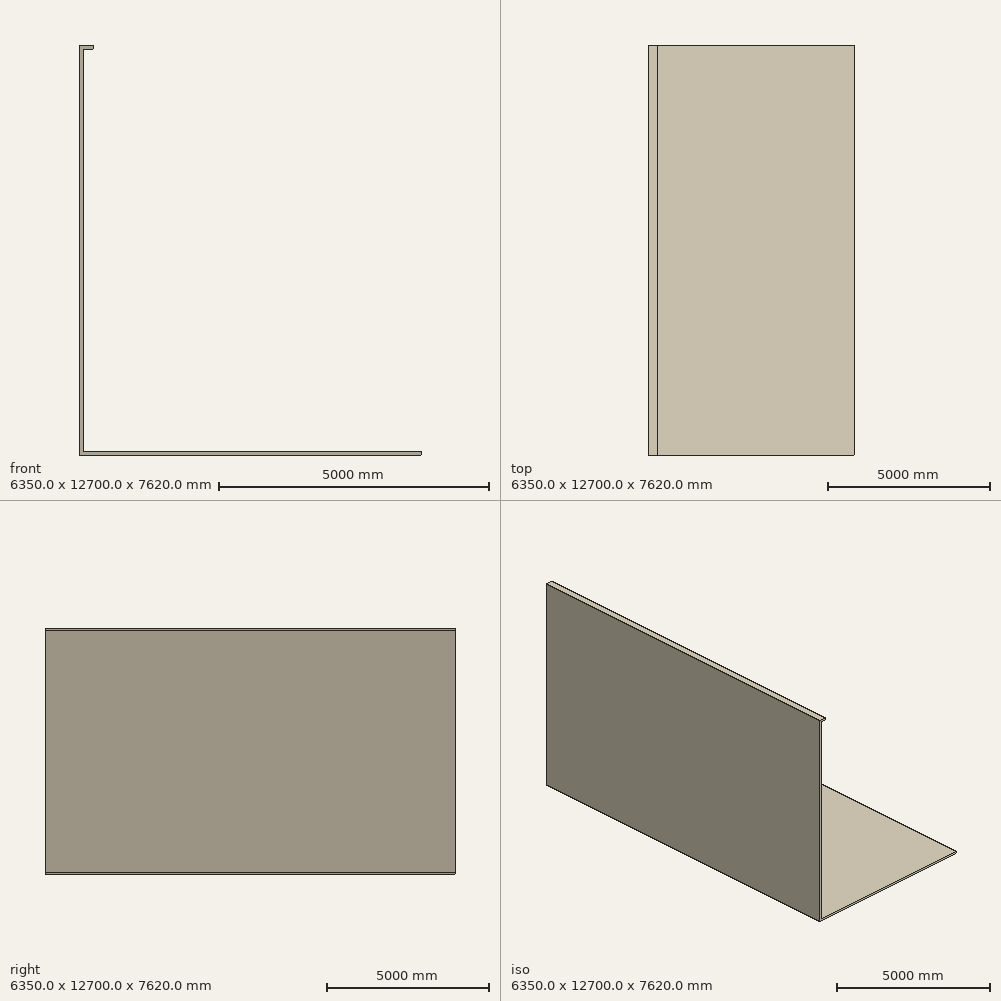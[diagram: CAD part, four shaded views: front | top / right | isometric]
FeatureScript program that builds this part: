
annotation { "Feature Type Name" : "Feature", "Feature Type Description" : "" }
export const myFeature = defineFeature(function(context is Context, id is Id, definition is map)
    precondition{}
    {
        {
            var Q0;
            Q0=qCreatedBy(makeId("Front.planeOp"),FACE);
            var sketch = newSketch(context, id + "F0", { "sketchPlane" : qUnion([Q0])});
            skLineSegment(sketch, "E0", {"start": v(-6350, 7620) * mm, "end": v(-6096, 7620) * mm});
            skLineSegment(sketch, "E1", {"start": v(-6350, 7620) * mm, "end": v(-6350, 0) * mm});
            skLineSegment(sketch, "E2", {"start": v(-6350, 0) * mm, "end": v(0, 0) * mm});
            skLineSegment(sketch, "E3", {"start": v(0, 8069.98) * mm, "end": v(0, 0) * mm, "construction": true});
            skLineSegment(sketch, "E4.0", {"start": v(-6273.8, 76.2) * mm, "end": v(0, 76.2) * mm});
            skLineSegment(sketch, "E4.1", {"start": v(-6273.8, 7543.8) * mm, "end": v(-6273.8, 76.2) * mm});
            skLineSegment(sketch, "E4.2", {"start": v(-6273.8, 7543.8) * mm, "end": v(-6096, 7543.8) * mm});
            skLineSegment(sketch, "E5", {"start": v(-6096, 7620) * mm, "end": v(-6096, 7543.8) * mm});
            skLineSegment(sketch, "E6", {"start": v(0, 76.2) * mm, "end": v(0, 0) * mm});
            skSolve(sketch);
        }
        {
            var Q0;
            Q0 = qSketchRegion(id + "F0", true);
            extrude(context, id + "F1", {"entities" : qUnion([Q0]), "endBound" : BoundingType.SYMMETRIC, "oppositeDirection" : true, "depth" : 12700 * mm});
        }
    });
